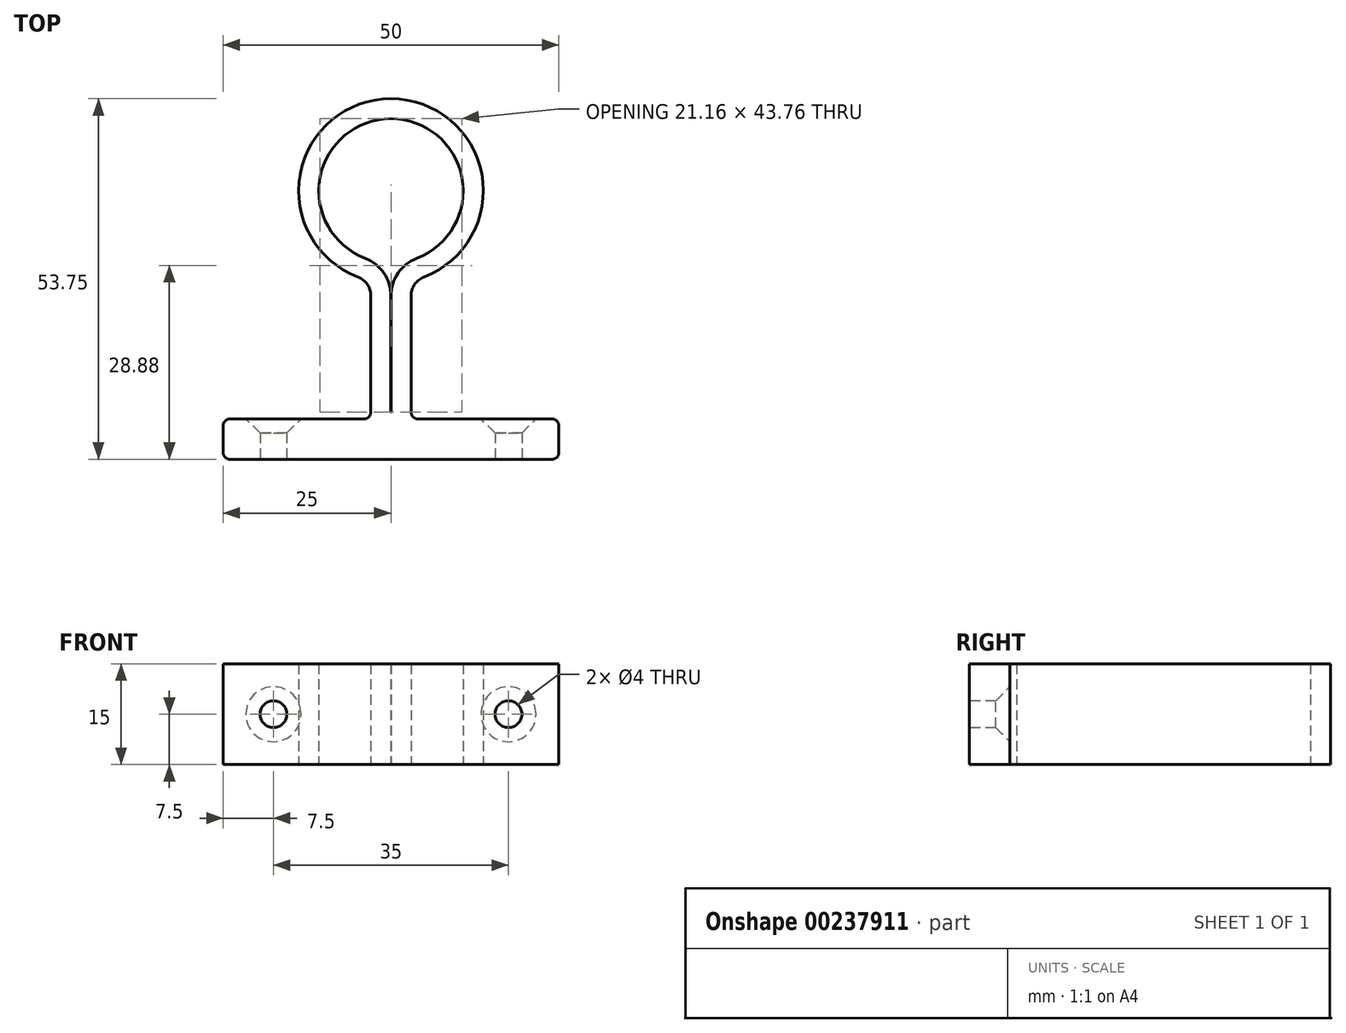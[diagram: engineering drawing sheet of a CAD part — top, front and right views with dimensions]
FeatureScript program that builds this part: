
annotation { "Feature Type Name" : "Feature", "Feature Type Description" : "" }
export const myFeature = defineFeature(function(context is Context, id is Id, definition is map)
    precondition{}
    {
        {
            var Q0;
            Q0=qCreatedBy(makeId("Top.planeOp"),FACE);
            var sketch = newSketch(context, id + "F0", { "sketchPlane" : qUnion([Q0])});
            skCircle(sketch, "E0", {"center": v(0, 0) * mm, "radius": 10.75 * mm, "construction": true});
            skArc(sketch, "E1", {"start": v(4.93, -12.84) * mm, "mid": v(0, 13.75) * mm, "end": v(-4.93, -12.84) * mm});
            skLineSegment(sketch, "E2.bottom", {"start": v(-24, -40) * mm, "end": v(24, -40) * mm});
            skLineSegment(sketch, "E2.top", {"start": v(-24, -34) * mm, "end": v(-4, -34) * mm});
            skLineSegment(sketch, "E2.left", {"start": v(-25, -39) * mm, "end": v(-25, -35) * mm});
            skLineSegment(sketch, "E2.right", {"start": v(25, -39) * mm, "end": v(25, -35) * mm});
            skLineSegment(sketch, "E3", {"start": v(-3, -33) * mm, "end": v(-3, -15.64) * mm});
            skLineSegment(sketch, "E4", {"start": v(3, -33) * mm, "end": v(3, -15.64) * mm});
            skLineSegment(sketch, "E5.trimOffspring", {"start": v(4, -34) * mm, "end": v(24, -34) * mm});
            skPoint(sketch, "E6.visualSharp", {"position": v(-3, -13.42) * mm});
            skArc(sketch, "E6.filletArc", {"start": v(-3, -15.64) * mm, "mid": v(-3.53, -13.94) * mm, "end": v(-4.93, -12.84) * mm});
            skPoint(sketch, "E7.visualSharp", {"position": v(-3, -34) * mm});
            skArc(sketch, "E7.filletArc", {"start": v(-4, -34) * mm, "mid": v(-3.3, -33.7) * mm, "end": v(-3, -33) * mm});
            skPoint(sketch, "E8.visualSharp", {"position": v(-25, -34) * mm});
            skArc(sketch, "E8.filletArc", {"start": v(-24, -34) * mm, "mid": v(-24.7, -34.3) * mm, "end": v(-25, -35) * mm});
            skPoint(sketch, "E9.visualSharp", {"position": v(-25, -40) * mm});
            skArc(sketch, "E9.filletArc", {"start": v(-25, -39) * mm, "mid": v(-24.7, -39.7) * mm, "end": v(-24, -40) * mm});
            skPoint(sketch, "E10.visualSharp", {"position": v(25, -40) * mm});
            skArc(sketch, "E10.filletArc", {"start": v(24, -40) * mm, "mid": v(24.7, -39.7) * mm, "end": v(25, -39) * mm});
            skPoint(sketch, "E11.visualSharp", {"position": v(25, -34) * mm});
            skArc(sketch, "E11.filletArc", {"start": v(25, -35) * mm, "mid": v(24.7, -34.3) * mm, "end": v(24, -34) * mm});
            skPoint(sketch, "E12.visualSharp", {"position": v(3, -34) * mm});
            skArc(sketch, "E12.filletArc", {"start": v(3, -33) * mm, "mid": v(3.3, -33.7) * mm, "end": v(4, -34) * mm});
            skPoint(sketch, "E13.visualSharp", {"position": v(3, -13.42) * mm});
            skArc(sketch, "E13.filletArc", {"start": v(4.93, -12.84) * mm, "mid": v(3.53, -13.94) * mm, "end": v(3, -15.64) * mm});
            skArc(sketch, "E14.0", {"start": v(3.85, -10.05) * mm, "mid": v(1.06, -12.25) * mm, "end": v(0.01, -15.64) * mm});
            skLineSegment(sketch, "E14.1", {"start": v(-22.01, -37) * mm, "end": v(-4, -37) * mm});
            skArc(sketch, "E14.2", {"start": v(-4, -37) * mm, "mid": v(-1.18, -35.82) * mm, "end": v(-0.01, -33) * mm});
            skLineSegment(sketch, "E14.3", {"start": v(0, -33) * mm, "end": v(-0.01, -15.64) * mm});
            skArc(sketch, "E14.4", {"start": v(0, -15.64) * mm, "mid": v(-1.06, -12.25) * mm, "end": v(-3.85, -10.05) * mm});
            skLineSegment(sketch, "E14.5", {"start": v(-22.01, -37.01) * mm, "end": v(-22.01, -37) * mm});
            skArc(sketch, "E14.6", {"start": v(3.85, -10.05) * mm, "mid": v(0, 10.76) * mm, "end": v(-3.85, -10.05) * mm});
            skLineSegment(sketch, "E14.7", {"start": v(-22.01, -37) * mm, "end": v(22.01, -37) * mm});
            skLineSegment(sketch, "E14.8", {"start": v(22.01, -37.01) * mm, "end": v(22.01, -37) * mm});
            skLineSegment(sketch, "E14.9", {"start": v(4, -37) * mm, "end": v(22.01, -37) * mm});
            skArc(sketch, "E14.10", {"start": v(0.01, -33) * mm, "mid": v(1.18, -35.82) * mm, "end": v(4, -36.99) * mm});
            skLineSegment(sketch, "E14.11", {"start": v(0, -33) * mm, "end": v(0.01, -15.64) * mm});
            skLineSegment(sketch, "E15", {"start": v(0.01, -33) * mm, "end": v(-0.01, -33) * mm});
            skSolve(sketch);
        }
        {
            var Q0;
            Q0=makeQuery(id+"F0.imprint","IMPRINT",FACE,{"disambiguationData":[TD([[makeQuery(id+"F0.imprint","IMPRINT",EDGE,{"derivedFrom":sQuery(id+"F0.wireOp",EDGE,"E1")}),1.0]])]});
            var Q1;
            Q1=makeQuery(id+"F0.imprint","IMPRINT",FACE,{"disambiguationData":[TD([[makeQuery(id+"F0.imprint","IMPRINT",EDGE,{"derivedFrom":sQuery(id+"F0.wireOp",EDGE,"E14.1")}),-1.0]])]});
            extrude(context, id + "F1", {"entities" : qUnion([Q0, Q1]), "depth" : 15 * mm, "offsetDistance" : 25 * mm});
        }
        {
            var Q0;
            Q0=makeQuery(id+"F1.opExtrude","SWEPT_FACE",FACE,{"disambiguationData":[OSD([sQuery(id+"F0.wireOp",EDGE,"E5.trimOffspring")])]});
            var sketch = newSketch(context, id + "F2", { "sketchPlane" : qUnion([Q0])});
            skPoint(sketch, "E16", {"position": v(-17.5, 7.5) * mm});
            skPoint(sketch, "E17", {"position": v(17.5, 7.5) * mm});
            skLineSegment(sketch, "E18", {"start": v(-17.5, 15) * mm, "end": v(-17.5, 0) * mm, "construction": true});
            skSolve(sketch);
        }
        {
            var Q0;
            Q0=sQuery(id+"F2.wireOp",VERTEX,"E16");
            var Q1;
            Q1=sQuery(id+"F2.wireOp",VERTEX,"E17");
            var Q2;
            Q2=makeQuery(id+"F1.opExtrude","SWEPT_BODY",BODY,{"disambiguationData":[OSD([sQuery(id+"F0.wireOp",EDGE,"E1"),sQuery(id+"F0.wireOp",EDGE,"E2.bottom"),sQuery(id+"F0.wireOp",EDGE,"E2.top"),sQuery(id+"F0.wireOp",EDGE,"E2.left"),sQuery(id+"F0.wireOp",EDGE,"E2.right"),sQuery(id+"F0.wireOp",EDGE,"E3"),sQuery(id+"F0.wireOp",EDGE,"E4"),sQuery(id+"F0.wireOp",EDGE,"E5.trimOffspring"),sQuery(id+"F0.wireOp",EDGE,"E6.filletArc"),sQuery(id+"F0.wireOp",EDGE,"E7.filletArc"),sQuery(id+"F0.wireOp",EDGE,"E8.filletArc"),sQuery(id+"F0.wireOp",EDGE,"E9.filletArc"),sQuery(id+"F0.wireOp",EDGE,"E10.filletArc"),sQuery(id+"F0.wireOp",EDGE,"E11.filletArc"),sQuery(id+"F0.wireOp",EDGE,"E12.filletArc"),sQuery(id+"F0.wireOp",EDGE,"E13.filletArc"),sQuery(id+"F0.wireOp",EDGE,"E14.0"),sQuery(id+"F0.wireOp",EDGE,"E14.1"),sQuery(id+"F0.wireOp",EDGE,"E14.2"),sQuery(id+"F0.wireOp",EDGE,"E14.3"),sQuery(id+"F0.wireOp",EDGE,"E14.4"),sQuery(id+"F0.wireOp",EDGE,"E14.5"),sQuery(id+"F0.wireOp",EDGE,"E14.6"),sQuery(id+"F0.wireOp",EDGE,"E14.7"),sQuery(id+"F0.wireOp",EDGE,"E14.8"),sQuery(id+"F0.wireOp",EDGE,"E14.9"),sQuery(id+"F0.wireOp",EDGE,"E14.10"),sQuery(id+"F0.wireOp",EDGE,"E14.11")])]});
            hole(context, id + "F3", {"style" : HoleStyle.C_SINK, "endStyle" : HoleEndStyle.BLIND, "standardTappedOrClearance" : lookupTablePath({ "standard" : "ISO", "size" : "4", "type" : "Drilled" }), "standardBlindInLast" : lookupTablePath({ "standard" : "ISO", "size" : "4", "type" : "Drilled" }), "holeDiameter" : 4 * mm, "cSinkDiameter" : 8.2 * mm, "cSinkAngle" : 90 * degree, "majorDiameter" : 5 * mm, "holeDepth" : 12 * mm, "isTappedThrough" : true, "tappedDepth" : 12 * mm, "tapClearance" : 3, "locations" : qUnion([Q0, Q1]), "scope" : qUnion([Q2]), "startStyle" : HoleStartStyle.PART});
        }
    });
